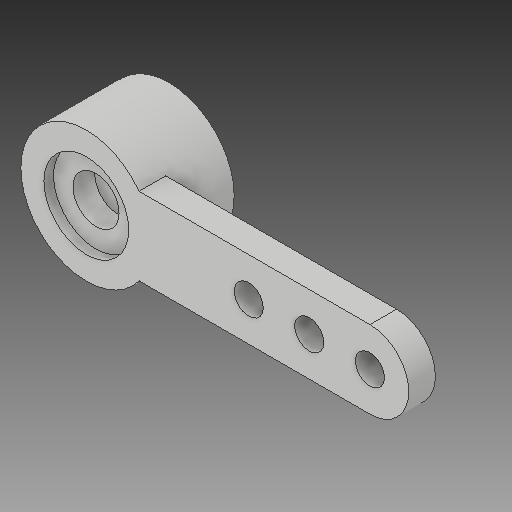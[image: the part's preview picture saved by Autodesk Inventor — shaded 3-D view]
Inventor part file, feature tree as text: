
AUTODESK INVENTOR PART (.ipt)
format: ipt  version: 2018.1 (Build 221171000, 171)  size: 150,016 bytes
history: native  units: mm
features: extrude x5, sketch x5, other x1
ambient origin geometry x8: Origin, YZ Plane, XZ Plane, XY Plane, X Axis, Y Axis, Z Axis, Center Point
bodies: Body1 (feature_tree)
feature tree (11):
  other  "ソリッド1"
  extrude  "押し出し1"  Depth=5.4mm
  extrude  "押し出し2"  Depth=1.9mm
  extrude  "押し出し3"  Depth=3.4mm TaperAngle=0.0deg
  extrude  "押し出し4"  Depth=3.5mm
  extrude  "押し出し5"  Depth=0.4mm TaperAngle=0.0deg
  sketch  "スケッチ1"
  sketch  "スケッチ2"
  sketch  "スケッチ3"
  sketch  "スケッチ4"
  sketch  "スケッチ5"
